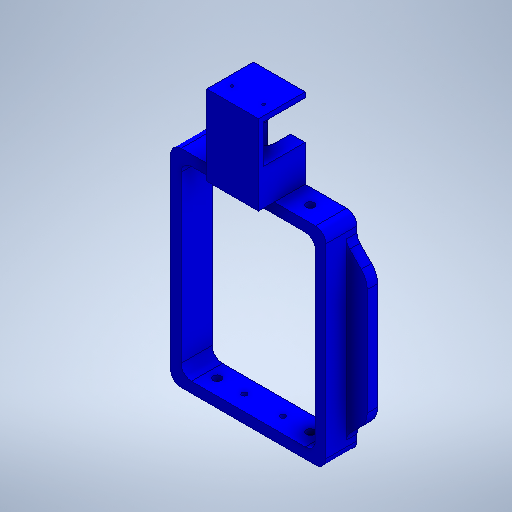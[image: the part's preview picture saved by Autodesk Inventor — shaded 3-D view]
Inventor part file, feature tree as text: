
AUTODESK INVENTOR PART (.ipt)
format: ipt  version: 2025.2 (Build 292293000, 293)  size: 415,744 bytes
history: native  units: mm
features: sketch x8, extrude x6, hole x5, fillet x3, other x1
ambient origin geometry x8: Origin, YZ Plane, XZ Plane, XY Plane, X Axis, Y Axis, Z Axis, Center Point
bodies: Solid1 (feature_tree)
feature tree (23):
  sketch  "Sketch1"  dims[d0=150.0mm d1=200.0mm]
  extrude  "Extrusion1"  Depth=200.0mm
  extrude  "Extrusion2"  Depth=10.0mm
  fillet  "Fillet1"  Radius=130.0mm
  sketch  "Sketch2"  dims[d2=10.0mm d3=10.0mm d4=130.0mm]
  hole  "Hole1"  [1 undecoded]
  hole  "Hole2"  [1 undecoded]
  hole  "Hole3"  [1 undecoded]
  hole  "Hole4"  [1 undecoded]
  sketch  "Sketch3"  dims[d5=180.0mm d6=40.0mm]
  other  "Work Axis1"
  sketch  "Sketch4"  dims[d7=20.0mm d8=40.0mm]
  extrude  "Extrusion3"  Depth=10.0mm
  sketch  "Sketch6"  dims[d11=40.0mm d12=30.0mm d13=0.0mm]
  extrude  "Extrusion4"  Depth=10.0mm
  extrude  "Extrusion5"  Depth=10.0mm
  hole  "Hole5"  [1 undecoded]
  fillet  "Fillet2"  Radius=15.0mm
  fillet  "Fillet3"  Radius=35.0mm
  extrude  "Extrusion6"  Depth=10.0mm
  sketch  "Sketch5"  dims[d9=40.0mm d10=20.0mm]
  sketch  "Sketch7"  dims[d14=10.0mm d15=0.0mm d16=20.0mm]
  sketch  "Sketch8"  dims[d17=20.0mm d18=20.0mm d19=8.0mm d20=6.0mm d21=4.0mm d22=2.0mm d23=90.0deg d24=5.0mm d25=0.0mm d26=8.0mm d27=6.0mm d28=4.0mm d29=2.0mm d30=90.0deg d31=5.0mm d32=0.0mm d33=37.3mm d34=5.0mm d35=6.0mm d36=4.0mm d37=2.0mm d38=90.0deg d39=8.0mm d40=0.0mm d41=22.0mm d42=6.0mm d43=4.0mm d44=2.0mm d45=90.0deg d46=8.0mm d47=0.0mm d48=30.0mm d49=15.0mm d50=35.0mm d51=0.0mm d52=50.0mm d53=15.0mm d54=50.0mm d55=5.0mm d56=43.5mm d57=45.0deg d58=37.3mm d59=0.0mm d60=50.0mm d61=5.0mm d62=0.0mm d63=3.0mm d64=6.0mm d65=4.0mm d66=2.0mm d67=90.0deg d68=8.0mm d69=20.594885mm d70=10.0mm d71=10.0mm d72=0.05mm d73=50.0mm d74=0.0mm]
note: 5 required parameter values undecoded (feature->parameter linkage not recoverable at this tier; creation-order binding heuristic only, values carry confidence <= 0.55)
